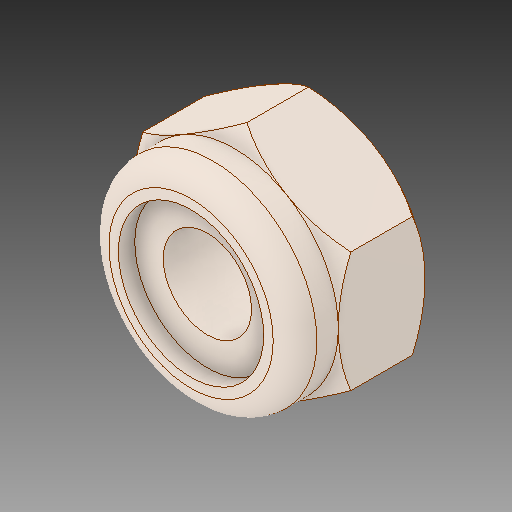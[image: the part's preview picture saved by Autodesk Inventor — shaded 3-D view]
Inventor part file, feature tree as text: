
AUTODESK INVENTOR PART (.ipt)
format: ipt  version: 2019 (Build 230136000, 136)  size: 167,936 bytes
history: native  units: in
note: dims shown in document units (in); Inventor stores cm internally (conversion verified against a paired STEP export)
features: fillet x1
ambient origin geometry x8: Origin, YZ Plane, XZ Plane, XY Plane, X Axis, Y Axis, Z Axis, Center Point
bodies: Solid1 (feature_tree)
feature tree (1):
  fillet  "Fillet1"  [1 undecoded]
note: 1 required parameter value undecoded (feature->parameter linkage not recoverable at this tier; creation-order binding heuristic only, values carry confidence <= 0.55)
